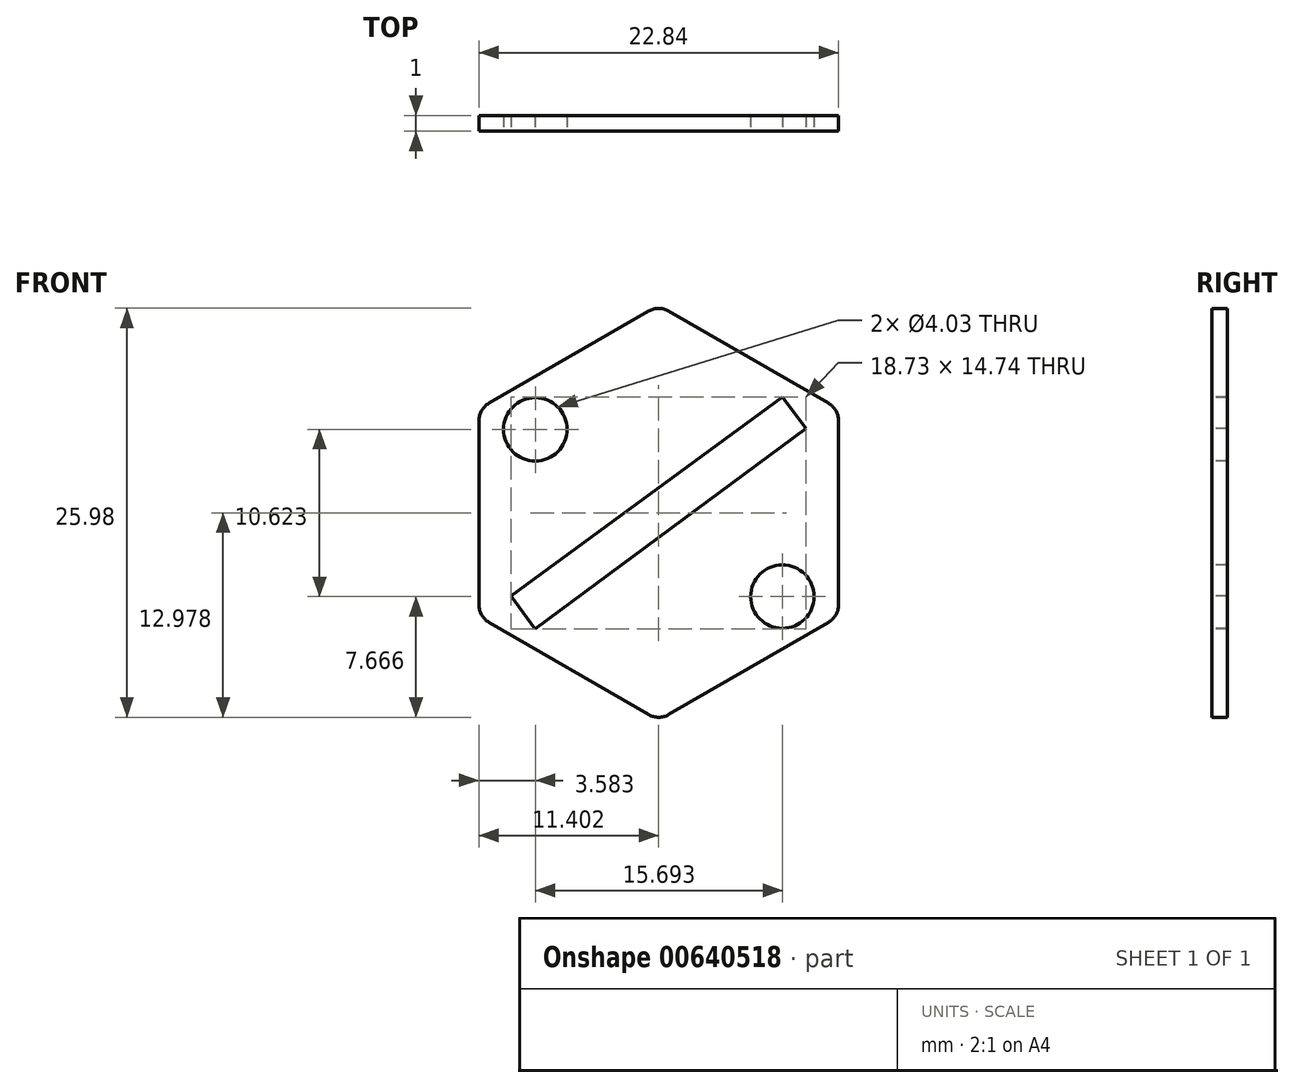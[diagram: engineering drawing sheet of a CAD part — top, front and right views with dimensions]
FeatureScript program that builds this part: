
annotation { "Feature Type Name" : "Feature", "Feature Type Description" : "" }
export const myFeature = defineFeature(function(context is Context, id is Id, definition is map)
    precondition{}
    {
        {
            var Q0;
            Q0=qCreatedBy(makeId("Front.planeOp"),FACE);
            var sketch = newSketch(context, id + "F0", { "sketchPlane" : qUnion([Q0])});
            skCircle(sketch, "E0.cCircle", {"center": v(0, 0) * mm, "radius": 12.7 * mm, "construction": true});
            skLineSegment(sketch, "E0.0", {"start": v(0.63, 14.3) * mm, "end": v(12.07, 7.7) * mm});
            skLineSegment(sketch, "E0.1", {"start": v(12.7, 6.6) * mm, "end": v(12.7, -6.6) * mm});
            skLineSegment(sketch, "E0.2", {"start": v(12.07, -7.7) * mm, "end": v(0.63, -14.3) * mm});
            skLineSegment(sketch, "E0.3", {"start": v(-0.64, -14.3) * mm, "end": v(-12.06, -7.7) * mm});
            skLineSegment(sketch, "E0.4", {"start": v(-12.7, -6.6) * mm, "end": v(-12.7, 6.6) * mm});
            skLineSegment(sketch, "E0.5", {"start": v(-12.07, 7.7) * mm, "end": v(-0.64, 14.3) * mm});
            skPoint(sketch, "E0.0.midPoint", {"position": v(6.35, 11) * mm});
            skPoint(sketch, "E1.visualSharp", {"position": v(0, 14.66) * mm});
            skArc(sketch, "E1.filletArc", {"start": v(0.63, 14.3) * mm, "mid": v(0, 14.47) * mm, "end": v(-0.64, 14.3) * mm});
            skPoint(sketch, "E2.visualSharp", {"position": v(-12.7, 7.33) * mm});
            skArc(sketch, "E2.filletArc", {"start": v(-12.07, 7.7) * mm, "mid": v(-12.53, 7.23) * mm, "end": v(-12.7, 6.6) * mm});
            skPoint(sketch, "E3.visualSharp", {"position": v(12.7, 7.33) * mm});
            skArc(sketch, "E3.filletArc", {"start": v(12.7, 6.6) * mm, "mid": v(12.53, 7.23) * mm, "end": v(12.07, 7.7) * mm});
            skPoint(sketch, "E4.visualSharp", {"position": v(12.7, -7.33) * mm});
            skArc(sketch, "E4.filletArc", {"start": v(12.07, -7.7) * mm, "mid": v(12.53, -7.23) * mm, "end": v(12.7, -6.6) * mm});
            skPoint(sketch, "E5.visualSharp", {"position": v(0, -14.66) * mm});
            skArc(sketch, "E5.filletArc", {"start": v(-0.64, -14.3) * mm, "mid": v(0, -14.47) * mm, "end": v(0.63, -14.3) * mm});
            skPoint(sketch, "E6.visualSharp", {"position": v(-12.7, -7.33) * mm});
            skArc(sketch, "E6.filletArc", {"start": v(-12.7, -6.6) * mm, "mid": v(-12.53, -7.23) * mm, "end": v(-12.07, -7.7) * mm});
            skSolve(sketch);
        }
        {
            var Q0;
            Q0=makeQuery(id+"F0.imprint","IMPRINT",FACE,{"disambiguationData":[TD([[makeQuery(id+"F0.imprint","IMPRINT",EDGE,{"derivedFrom":sQuery(id+"F0.wireOp",EDGE,"E0.0")}),-1.0]])]});
            var sketch = newSketch(context, id + "F1", { "sketchPlane" : qUnion([Q0])});
            skCircle(sketch, "E7.cCircle", {"center": v(0, 0) * mm, "radius": 11.42 * mm, "construction": true});
            skLineSegment(sketch, "E7.0", {"start": v(0.64, 12.82) * mm, "end": v(10.78, 6.96) * mm});
            skLineSegment(sketch, "E7.1", {"start": v(11.42, 5.86) * mm, "end": v(11.42, -5.86) * mm});
            skLineSegment(sketch, "E7.2", {"start": v(10.78, -6.96) * mm, "end": v(0.63, -12.82) * mm});
            skLineSegment(sketch, "E7.3", {"start": v(-0.64, -12.82) * mm, "end": v(-10.78, -6.96) * mm});
            skLineSegment(sketch, "E7.4", {"start": v(-11.42, -5.86) * mm, "end": v(-11.42, 5.86) * mm});
            skLineSegment(sketch, "E7.5", {"start": v(-10.78, 6.96) * mm, "end": v(-0.63, 12.82) * mm});
            skPoint(sketch, "E7.0.midPoint", {"position": v(5.7, 9.89) * mm});
            skPoint(sketch, "E8.visualSharp", {"position": v(0, 13.18) * mm});
            skArc(sketch, "E8.filletArc", {"start": v(0.64, 12.82) * mm, "mid": v(0, 12.99) * mm, "end": v(-0.63, 12.82) * mm});
            skPoint(sketch, "E9.visualSharp", {"position": v(-11.42, 6.6) * mm});
            skArc(sketch, "E9.filletArc", {"start": v(-10.78, 6.96) * mm, "mid": v(-11.25, 6.5) * mm, "end": v(-11.42, 5.86) * mm});
            skPoint(sketch, "E10.visualSharp", {"position": v(11.42, 6.6) * mm});
            skArc(sketch, "E10.filletArc", {"start": v(11.42, 5.86) * mm, "mid": v(11.25, 6.5) * mm, "end": v(10.78, 6.96) * mm});
            skPoint(sketch, "E11.visualSharp", {"position": v(11.42, -6.6) * mm});
            skArc(sketch, "E11.filletArc", {"start": v(10.78, -6.96) * mm, "mid": v(11.25, -6.5) * mm, "end": v(11.42, -5.86) * mm});
            skPoint(sketch, "E12.visualSharp", {"position": v(0, -13.18) * mm});
            skArc(sketch, "E12.filletArc", {"start": v(-0.64, -12.82) * mm, "mid": v(0, -12.99) * mm, "end": v(0.64, -12.82) * mm});
            skPoint(sketch, "E13.visualSharp", {"position": v(-11.42, -6.6) * mm});
            skArc(sketch, "E13.filletArc", {"start": v(-11.42, -5.86) * mm, "mid": v(-11.25, -6.5) * mm, "end": v(-10.78, -6.96) * mm});
            skSolve(sketch);
        }
        {
            var Q0;
            Q0 = qSketchRegion(id + "F1", true);
            extrude(context, id + "F2", {"entities" : qUnion([Q0]), "depth" : 1 * mm, "offsetDistance" : 25.4 * mm, "symmetric" : true});
        }
        {
            var Q0;
            Q0=makeQuery(id+"F2.opExtrude","CAP_FACE",FACE,{"disambiguationData":[OSD([sQuery(id+"F1.wireOp",EDGE,"E7.0"),sQuery(id+"F1.wireOp",EDGE,"E7.1"),sQuery(id+"F1.wireOp",EDGE,"E7.2"),sQuery(id+"F1.wireOp",EDGE,"E7.3"),sQuery(id+"F1.wireOp",EDGE,"E7.4"),sQuery(id+"F1.wireOp",EDGE,"E7.5"),sQuery(id+"F1.wireOp",EDGE,"E8.filletArc"),sQuery(id+"F1.wireOp",EDGE,"E9.filletArc"),sQuery(id+"F1.wireOp",EDGE,"E10.filletArc"),sQuery(id+"F1.wireOp",EDGE,"E11.filletArc"),sQuery(id+"F1.wireOp",EDGE,"E12.filletArc"),sQuery(id+"F1.wireOp",EDGE,"E13.filletArc")])],"isStart":false});
            var sketch = newSketch(context, id + "F3", { "sketchPlane" : qUnion([Q0])});
            skCircle(sketch, "E14", {"center": v(-7.84, 5.3) * mm, "radius": 2.01 * mm});
            skCircle(sketch, "E15.MirrorC", {"center": v(7.86, -5.32) * mm, "radius": 2.01 * mm});
            skLineSegment(sketch, "E16.0", {"start": v(7.86, 7.36) * mm, "end": v(9.35, 5.35) * mm});
            skLineSegment(sketch, "E16.1", {"start": v(-9.38, -5.3) * mm, "end": v(7.86, 7.36) * mm});
            skLineSegment(sketch, "E16.2", {"start": v(-7.84, -7.38) * mm, "end": v(-9.38, -5.3) * mm});
            skLineSegment(sketch, "E16.3", {"start": v(9.35, 5.35) * mm, "end": v(-7.84, -7.38) * mm});
            skSolve(sketch);
        }
        {
            var Q0;
            Q0 = qSketchRegion(id + "F3", true);
            extrude(context, id + "F4", {"entities" : qUnion([Q0]), "operationType" : NewBodyOperationType.REMOVE, "endBound" : BoundingType.THROUGH_ALL, "oppositeDirection" : true, "depth" : 25.4 * mm, "offsetDistance" : 25.4 * mm});
        }
    });
